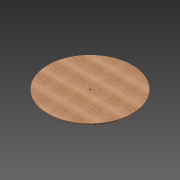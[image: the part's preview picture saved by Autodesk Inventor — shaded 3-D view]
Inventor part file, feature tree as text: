
AUTODESK INVENTOR PART (.ipt)
format: ipt  version: 2013 (Build 170138000, 138)  size: 91,136 bytes
history: native  units: in
note: dims shown in document units (in); Inventor stores cm internally (conversion verified against a paired STEP export)
features: extrude x1, sketch x1
ambient origin geometry x8: Origin, YZ Plane, XZ Plane, XY Plane, X Axis, Y Axis, Z Axis, Center Point
bodies: Solid1 (feature_tree)
feature tree (2):
  extrude  "Extrusion1"  Depth=0.75in TaperAngle=0.0deg
  sketch  "Sketch1"  dims[d0=48.0in d2=0.75in d3=0.0in d5=1.0in d6=0.205in d7=23.5in d8=1.5748in d10=360.0deg]
